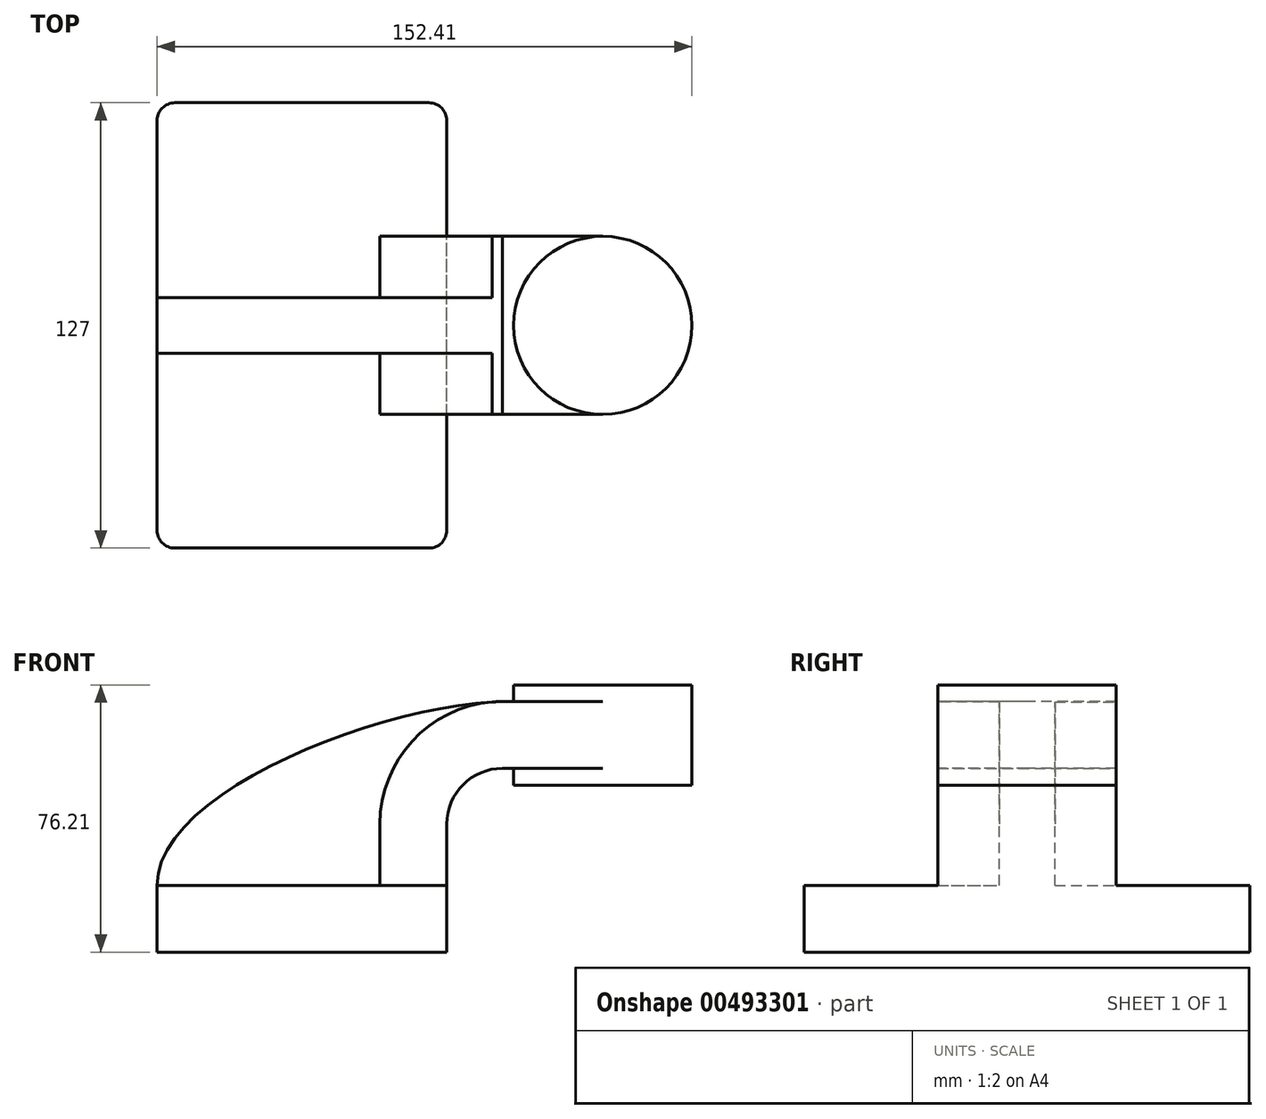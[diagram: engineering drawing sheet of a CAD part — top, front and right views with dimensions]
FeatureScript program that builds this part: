
annotation { "Feature Type Name" : "Feature", "Feature Type Description" : "" }
export const myFeature = defineFeature(function(context is Context, id is Id, definition is map)
    precondition{}
    {
        {
            var Q0;
            Q0=qCreatedBy(makeId("Front.planeOp"),FACE);
            var sketch = newSketch(context, id + "F0", { "sketchPlane" : qUnion([Q0])});
            skLineSegment(sketch, "E0.bottom", {"start": v(-41.28, 9.52) * mm, "end": v(41.28, 9.53) * mm});
            skLineSegment(sketch, "E0.top", {"start": v(-41.28, -9.53) * mm, "end": v(41.28, -9.53) * mm});
            skLineSegment(sketch, "E0.left", {"start": v(-41.28, 9.52) * mm, "end": v(-41.27, -9.53) * mm});
            skLineSegment(sketch, "E0.right", {"start": v(41.28, 9.53) * mm, "end": v(41.28, -9.52) * mm});
            skPoint(sketch, "E0.middle", {"position": v(0, 0) * mm});
            skLineSegment(sketch, "E1.bottom", {"start": v(60.33, 38.1) * mm, "end": v(111.13, 38.1) * mm});
            skLineSegment(sketch, "E1.top", {"start": v(60.32, 66.67) * mm, "end": v(111.13, 66.67) * mm});
            skLineSegment(sketch, "E1.left", {"start": v(60.33, 38.1) * mm, "end": v(60.32, 66.67) * mm});
            skLineSegment(sketch, "E1.right", {"start": v(111.13, 38.1) * mm, "end": v(111.13, 66.67) * mm});
            skPoint(sketch, "E1.middle", {"position": v(85.73, 52.39) * mm});
            skLineSegment(sketch, "E2", {"start": v(41.27, 9.53) * mm, "end": v(41.27, 27) * mm});
            skArc(sketch, "E3", {"start": v(41.27, 27) * mm, "mid": v(45.92, 38.23) * mm, "end": v(57.15, 42.88) * mm});
            skLineSegment(sketch, "E4", {"start": v(57.15, 42.88) * mm, "end": v(86.13, 42.88) * mm});
            skLineSegment(sketch, "E5.0", {"start": v(57.15, 61.93) * mm, "end": v(86.13, 61.93) * mm});
            skArc(sketch, "E5.1", {"start": v(22.23, 27) * mm, "mid": v(32.45, 51.7) * mm, "end": v(57.15, 61.93) * mm});
            skLineSegment(sketch, "E5.2", {"start": v(22.22, 9.53) * mm, "end": v(22.22, 27) * mm});
            skLineSegment(sketch, "E6", {"start": v(85.73, 38.1) * mm, "end": v(85.73, 66.67) * mm});
            skFitSpline(sketch, "E7", {"points": [v(-41.28, 9.52) * mm, v(57.15, 61.93) * mm], "startDerivative": vector(-0.4, 81.08) * mm, "endDerivative": vector(102.06, 2.44) * mm});
            skSolve(sketch);
        }
        {
            var Q0;
            Q0=makeQuery(id+"F0.imprint","IMPRINT",FACE,{"disambiguationData":[TD([[makeQuery(id+"F0.imprint","IMPRINT",EDGE,{"derivedFrom":sQuery(id+"F0.wireOp",EDGE,"E0.top")}),1.0]])]});
            extrude(context, id + "F1", {"entities" : qUnion([Q0]), "endBound" : BoundingType.SYMMETRIC, "depth" : 127 * mm});
        }
        {
            var Q0;
            {var subQ1=sQuery(id+"F0.wireOp",EDGE,"E2");Q0=makeQuery(id+"F0.imprint","IMPRINT",FACE,{"disambiguationData":[TD([[makeQuery(id+"F0.imprint","IMPRINT",EDGE,{"derivedFrom":subQ1}),1.0]])]});}
            extrude(context, id + "F2", {"entities" : qUnion([Q0]), "operationType" : NewBodyOperationType.ADD, "endBound" : BoundingType.SYMMETRIC, "depth" : 50.8 * mm});
        }
        {
            var Q0;
            {var subQ0=sQuery(id+"F0.wireOp",EDGE,"E4");var subQ1=sQuery(id+"F0.wireOp",EDGE,"E1.left");var subQ2=makeQuery(id+"F0.imprint","INTERSECT",VERTEX,{"derivedFrom":[subQ1,subQ0]});Q0=makeQuery(id+"F0.imprint","IMPRINT",FACE,{"disambiguationData":[TD([[makeQuery(id+"F0.imprint","IMPRINT",EDGE,{"disambiguationData":[TD([[subQ2,-1.0]])],"derivedFrom":subQ1}),-1.0]])]});}
            extrude(context, id + "F3", {"entities" : qUnion([Q0]), "operationType" : NewBodyOperationType.ADD, "endBound" : BoundingType.SYMMETRIC, "depth" : 50.8 * mm});
        }
        {
            var Q0;
            {var subQ3=sQuery(id+"F0.wireOp",EDGE,"E5.2");Q0=makeQuery(id+"F0.imprint","IMPRINT",FACE,{"disambiguationData":[TD([[makeQuery(id+"F0.imprint","IMPRINT",EDGE,{"derivedFrom":subQ3}),1.0]])]});}
            extrude(context, id + "F4", {"entities" : qUnion([Q0]), "operationType" : NewBodyOperationType.ADD, "endBound" : BoundingType.SYMMETRIC, "depth" : 15.88 * mm});
        }
        {
            var Q0;
            {var subQ4=sQuery(id+"F0.wireOp",EDGE,"E1.right");Q0=makeQuery(id+"F0.imprint","IMPRINT",FACE,{"disambiguationData":[TD([[makeQuery(id+"F0.imprint","IMPRINT",EDGE,{"derivedFrom":subQ4}),1.0]])]});}
            var Q1;
            Q1=sQuery(id+"F0.wireOp",EDGE,"E6");
            revolve(context, id + "F5", {"operationType" : NewBodyOperationType.ADD, "entities" : qUnion([Q0]), "axis" : qUnion([Q1]), "revolveType" : RevolveType.FULL});
        }
        {
            var Q0;
            Q0=makeQuery(id+"F1.opExtrude","CAP_EDGE",EDGE,{"disambiguationData":[OSD([sQuery(id+"F0.wireOp",EDGE,"E0.left")])],"isStart":false});
            var Q1;
            Q1=makeQuery(id+"F1.opExtrude","CAP_EDGE",EDGE,{"disambiguationData":[OSD([sQuery(id+"F0.wireOp",EDGE,"E0.left")])],"isStart":true});
            var Q2;
            Q2=makeQuery(id+"F1.opExtrude","CAP_EDGE",EDGE,{"disambiguationData":[OSD([sQuery(id+"F0.wireOp",EDGE,"E0.right")])],"isStart":true});
            var Q3;
            Q3=makeQuery(id+"F1.opExtrude","CAP_EDGE",EDGE,{"disambiguationData":[OSD([sQuery(id+"F0.wireOp",EDGE,"E0.right")])],"isStart":false});
            fillet(context, id + "F6", {"entities" : qUnion([Q0, Q1, Q2, Q3]), "radius" : 5.08 * mm, "tangentPropagation" : true, "allowEdgeOverflow" : false});
        }
    });
